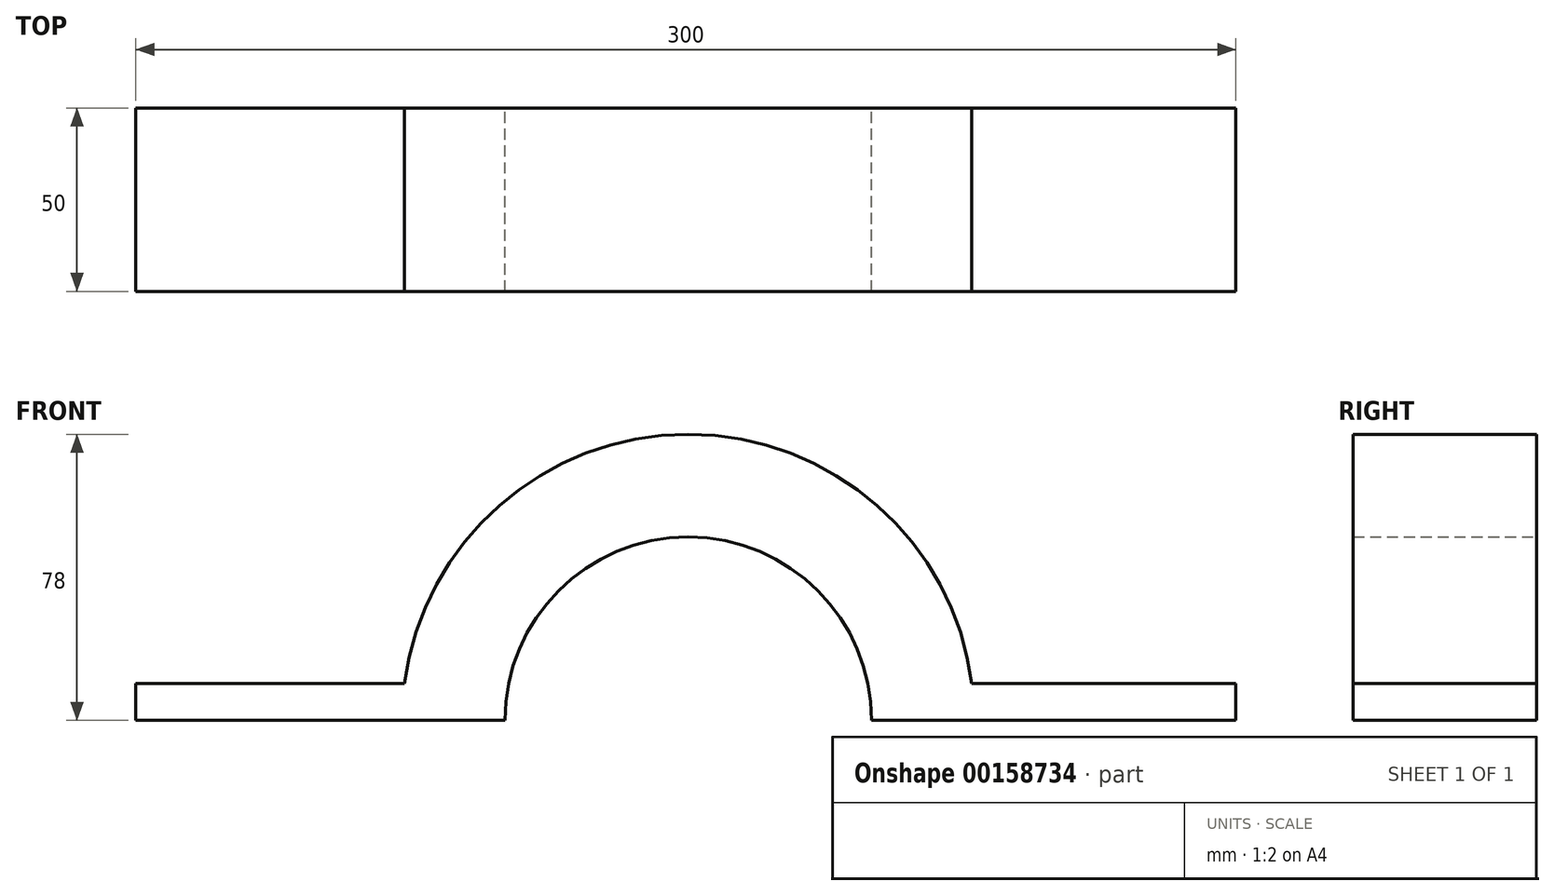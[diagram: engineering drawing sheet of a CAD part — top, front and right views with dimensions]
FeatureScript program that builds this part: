
annotation { "Feature Type Name" : "Feature", "Feature Type Description" : "" }
export const myFeature = defineFeature(function(context is Context, id is Id, definition is map)
    precondition{}
    {
        {
            var Q0;
            Q0=qCreatedBy(makeId("Front.planeOp"),FACE);
            var sketch = newSketch(context, id + "F0", { "sketchPlane" : qUnion([Q0])});
            skPoint(sketch, "E0.middle", {"position": v(0, 0) * mm});
            skArc(sketch, "E1", {"start": v(-50, 0) * mm, "mid": v(0, 50) * mm, "end": v(50, 0) * mm});
            skArc(sketch, "E2", {"start": v(-77.36, 10) * mm, "mid": v(0, 78) * mm, "end": v(77.36, 10) * mm});
            skLineSegment(sketch, "E3", {"start": v(50, 0) * mm, "end": v(149.36, 0) * mm});
            skLineSegment(sketch, "E4", {"start": v(149.36, 0) * mm, "end": v(149.36, 10) * mm});
            skLineSegment(sketch, "E5", {"start": v(149.36, 10) * mm, "end": v(77.36, 10) * mm});
            skLineSegment(sketch, "E6", {"start": v(-78, 0) * mm, "end": v(-150.64, 0) * mm});
            skLineSegment(sketch, "E7", {"start": v(-150.64, 0) * mm, "end": v(-150.64, 10) * mm});
            skLineSegment(sketch, "E8", {"start": v(-150.64, 10) * mm, "end": v(-77.36, 10) * mm});
            skLineSegment(sketch, "E9", {"start": v(-50, 0) * mm, "end": v(-78, 0) * mm});
            skPoint(sketch, "E10.orphan", {"position": v(78, 0) * mm});
            skSolve(sketch);
        }
        {
            var Q0;
            Q0 = qSketchRegion(id + "F0", true);
            extrude(context, id + "F1", {"entities" : qUnion([Q0]), "depth" : 50 * mm});
        }
    });
